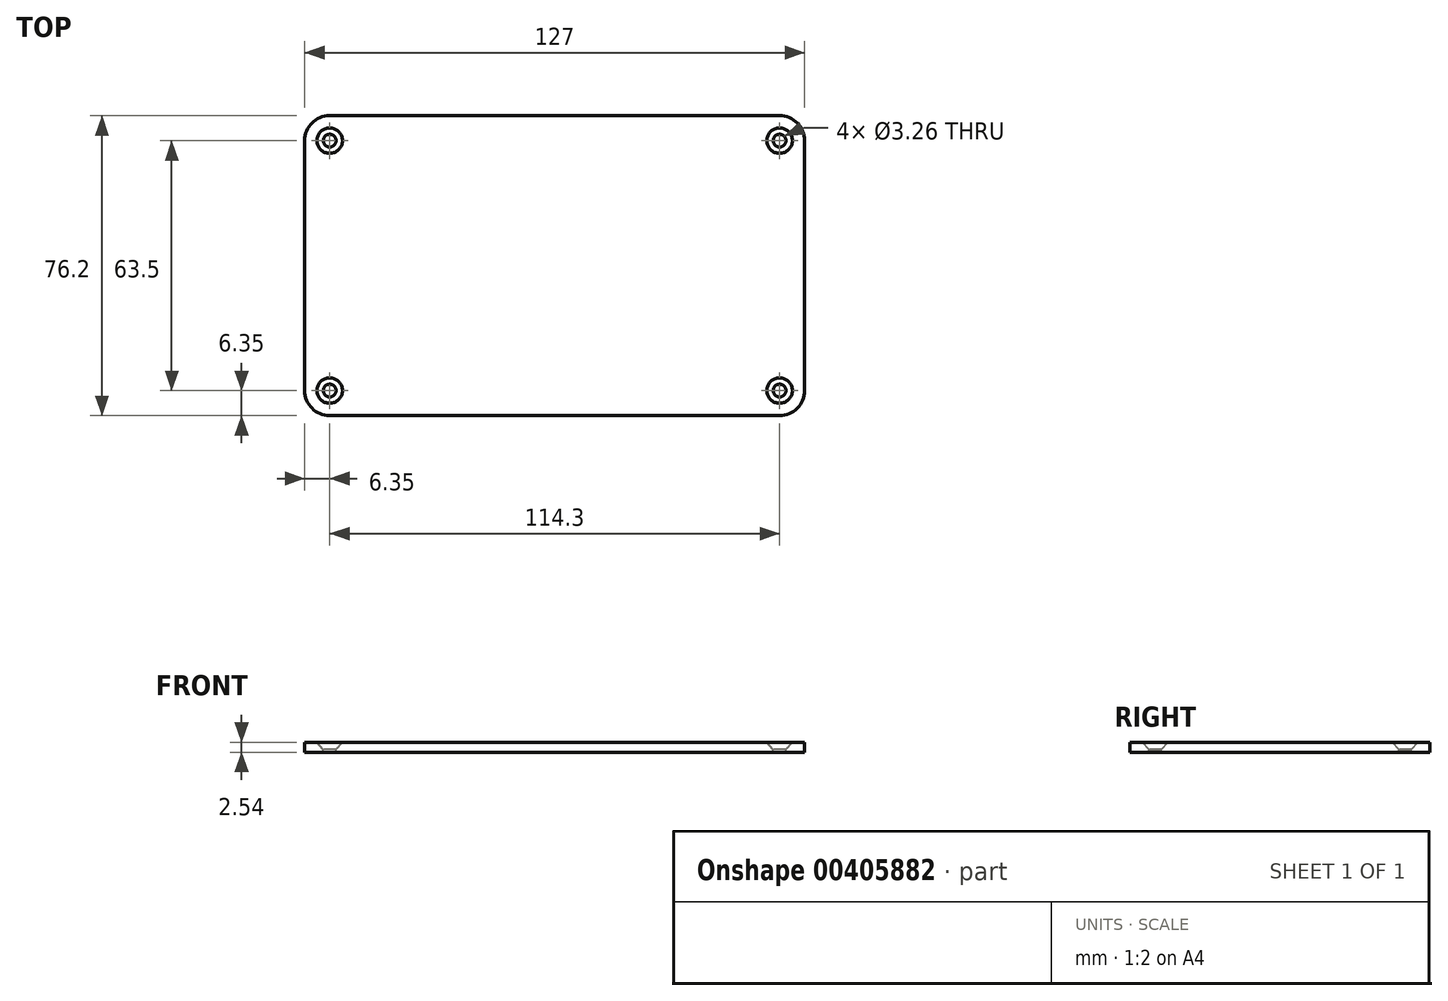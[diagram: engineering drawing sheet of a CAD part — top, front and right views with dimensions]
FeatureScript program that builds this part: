
annotation { "Feature Type Name" : "Feature", "Feature Type Description" : "" }
export const myFeature = defineFeature(function(context is Context, id is Id, definition is map)
    precondition{}
    {
        {
            var Q0;
            Q0=qCreatedBy(makeId("Top.planeOp"),FACE);
            var sketch = newSketch(context, id + "F0", { "sketchPlane" : qUnion([Q0])});
            skLineSegment(sketch, "E0.bottom", {"start": v(6.35, 76.2) * mm, "end": v(120.65, 76.2) * mm});
            skLineSegment(sketch, "E0.top", {"start": v(6.35, 0) * mm, "end": v(120.65, 0) * mm});
            skLineSegment(sketch, "E0.left", {"start": v(0, 69.85) * mm, "end": v(0, 6.35) * mm});
            skLineSegment(sketch, "E0.right", {"start": v(127, 69.85) * mm, "end": v(127, 6.35) * mm});
            skPoint(sketch, "E1.visualSharp", {"position": v(0, 76.2) * mm});
            skArc(sketch, "E1.filletArc", {"start": v(6.35, 76.2) * mm, "mid": v(1.86, 74.34) * mm, "end": v(0, 69.85) * mm});
            skPoint(sketch, "E2.visualSharp", {"position": v(127, 76.2) * mm});
            skArc(sketch, "E2.filletArc", {"start": v(127, 69.85) * mm, "mid": v(125.14, 74.34) * mm, "end": v(120.65, 76.2) * mm});
            skPoint(sketch, "E3.visualSharp", {"position": v(127, 0) * mm});
            skArc(sketch, "E3.filletArc", {"start": v(120.65, 0) * mm, "mid": v(125.14, 1.86) * mm, "end": v(127, 6.35) * mm});
            skPoint(sketch, "E4.visualSharp", {"position": v(0, 0) * mm});
            skArc(sketch, "E4.filletArc", {"start": v(0, 6.35) * mm, "mid": v(1.86, 1.86) * mm, "end": v(6.35, 0) * mm});
            skSolve(sketch);
        }
        {
            var Q0;
            Q0=makeQuery(id+"F0.imprint","IMPRINT",FACE,{"disambiguationData":[TD([[makeQuery(id+"F0.imprint","IMPRINT",EDGE,{"derivedFrom":sQuery(id+"F0.wireOp",EDGE,"E0.bottom")}),-1.0]])]});
            extrude(context, id + "F1", {"entities" : qUnion([Q0]), "depth" : 2.54 * mm});
        }
        {
            var Q0;
            Q0=makeQuery(id+"F1.opExtrude","CAP_FACE",FACE,{"disambiguationData":[OSD([sQuery(id+"F0.wireOp",EDGE,"E0.bottom"),sQuery(id+"F0.wireOp",EDGE,"E0.top"),sQuery(id+"F0.wireOp",EDGE,"E0.left"),sQuery(id+"F0.wireOp",EDGE,"E0.right"),sQuery(id+"F0.wireOp",EDGE,"E1.filletArc"),sQuery(id+"F0.wireOp",EDGE,"E2.filletArc"),sQuery(id+"F0.wireOp",EDGE,"E3.filletArc"),sQuery(id+"F0.wireOp",EDGE,"E4.filletArc")])],"isStart":false});
            var sketch = newSketch(context, id + "F2", { "sketchPlane" : qUnion([Q0])});
            skPoint(sketch, "E5", {"position": v(6.35, 6.35) * mm});
            skPoint(sketch, "E6", {"position": v(6.35, 69.85) * mm});
            skPoint(sketch, "E7", {"position": v(120.65, 6.35) * mm});
            skPoint(sketch, "E8", {"position": v(120.65, 69.85) * mm});
            skSolve(sketch);
        }
        {
            var Q0;
            Q0=sQuery(id+"F2.wireOp",VERTEX,"E6");
            var Q1;
            Q1=sQuery(id+"F2.wireOp",VERTEX,"E5");
            var Q2;
            Q2=sQuery(id+"F2.wireOp",VERTEX,"E7");
            var Q3;
            Q3=sQuery(id+"F2.wireOp",VERTEX,"E8");
            var Q4;
            Q4=makeQuery(id+"F1.opExtrude","SWEPT_BODY",BODY,{"disambiguationData":[OSD([sQuery(id+"F0.wireOp",EDGE,"E0.bottom"),sQuery(id+"F0.wireOp",EDGE,"E0.top"),sQuery(id+"F0.wireOp",EDGE,"E0.left"),sQuery(id+"F0.wireOp",EDGE,"E0.right"),sQuery(id+"F0.wireOp",EDGE,"E1.filletArc"),sQuery(id+"F0.wireOp",EDGE,"E2.filletArc"),sQuery(id+"F0.wireOp",EDGE,"E3.filletArc"),sQuery(id+"F0.wireOp",EDGE,"E4.filletArc")])]});
            hole(context, id + "F3", {"style" : HoleStyle.C_SINK, "endStyle" : HoleEndStyle.THROUGH, "standardTappedOrClearance" : lookupTablePath({ "standard" : "ANSI", "fit" : "Normal (ASME)", "size" : "#4", "type" : "Clearance" }), "standardBlindInLast" : lookupTablePath({ "fit" : "Free", "standard" : "ANSI", "size" : "#4", "type" : "Clearance" }), "holeDiameter" : 3.26 * mm, "cSinkDiameter" : 6.48 * mm, "cSinkAngle" : 82 * degree, "isTappedThrough" : true, "tappedDepth" : 12.7 * mm, "tapClearance" : 3, "locations" : qUnion([Q0, Q1, Q2, Q3]), "scope" : qUnion([Q4])});
        }
    });
